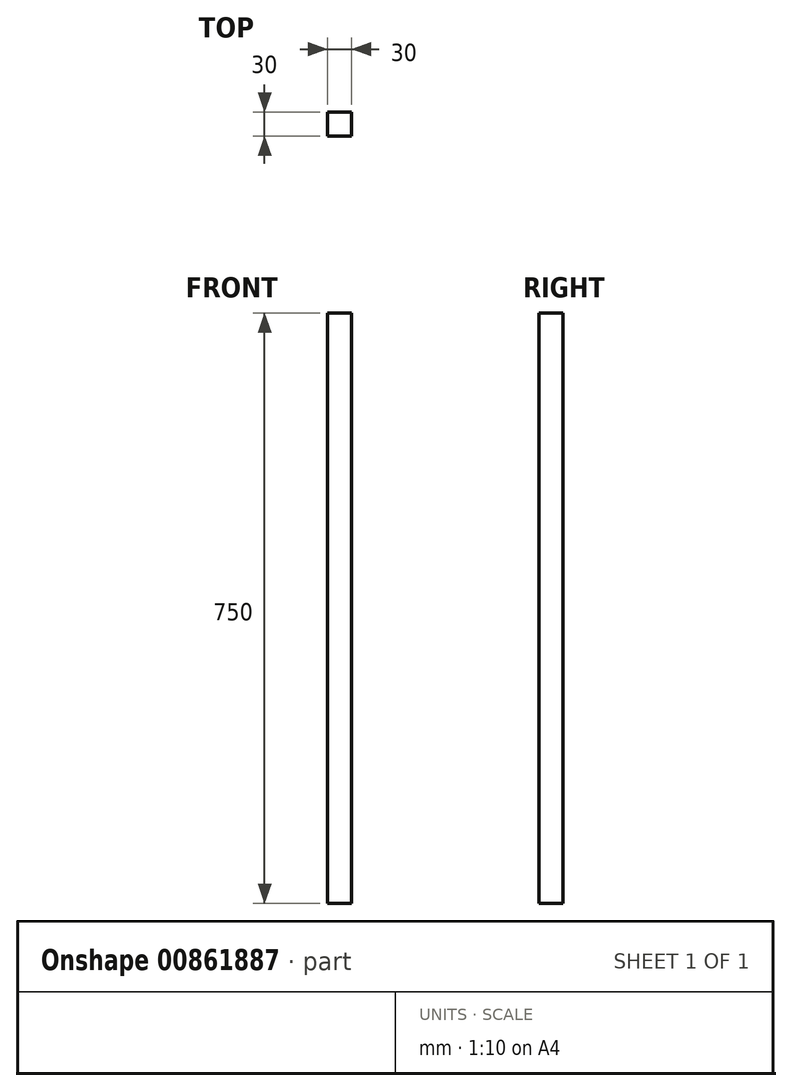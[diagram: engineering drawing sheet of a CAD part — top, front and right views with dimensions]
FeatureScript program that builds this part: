
annotation { "Feature Type Name" : "Feature", "Feature Type Description" : "" }
export const myFeature = defineFeature(function(context is Context, id is Id, definition is map)
    precondition{}
    {
        {
            var Q0;
            Q0=qCreatedBy(makeId("Top.planeOp"),FACE);
            var sketch = newSketch(context, id + "F0", { "sketchPlane" : qUnion([Q0])});
            skLineSegment(sketch, "E0.bottom", {"start": v(15, -15) * mm, "end": v(-15, -15) * mm});
            skLineSegment(sketch, "E0.top", {"start": v(15, 15) * mm, "end": v(-15, 15) * mm});
            skLineSegment(sketch, "E0.left", {"start": v(15, -15) * mm, "end": v(15, 15) * mm});
            skLineSegment(sketch, "E0.right", {"start": v(-15, -15) * mm, "end": v(-15, 15) * mm});
            skPoint(sketch, "E0.middle", {"position": v(0, 0) * mm});
            skSolve(sketch);
        }
        {
            var Q0;
            Q0=makeQuery(id+"F0.imprint","IMPRINT",FACE,{"disambiguationData":[TD([[makeQuery(id+"F0.imprint","IMPRINT",EDGE,{"derivedFrom":sQuery(id+"F0.wireOp",EDGE,"E0.bottom")}),-1.0]])]});
            extrude(context, id + "F1", {"entities" : qUnion([Q0]), "depth" : 750 * mm, "offsetDistance" : 25 * mm});
        }
    });
